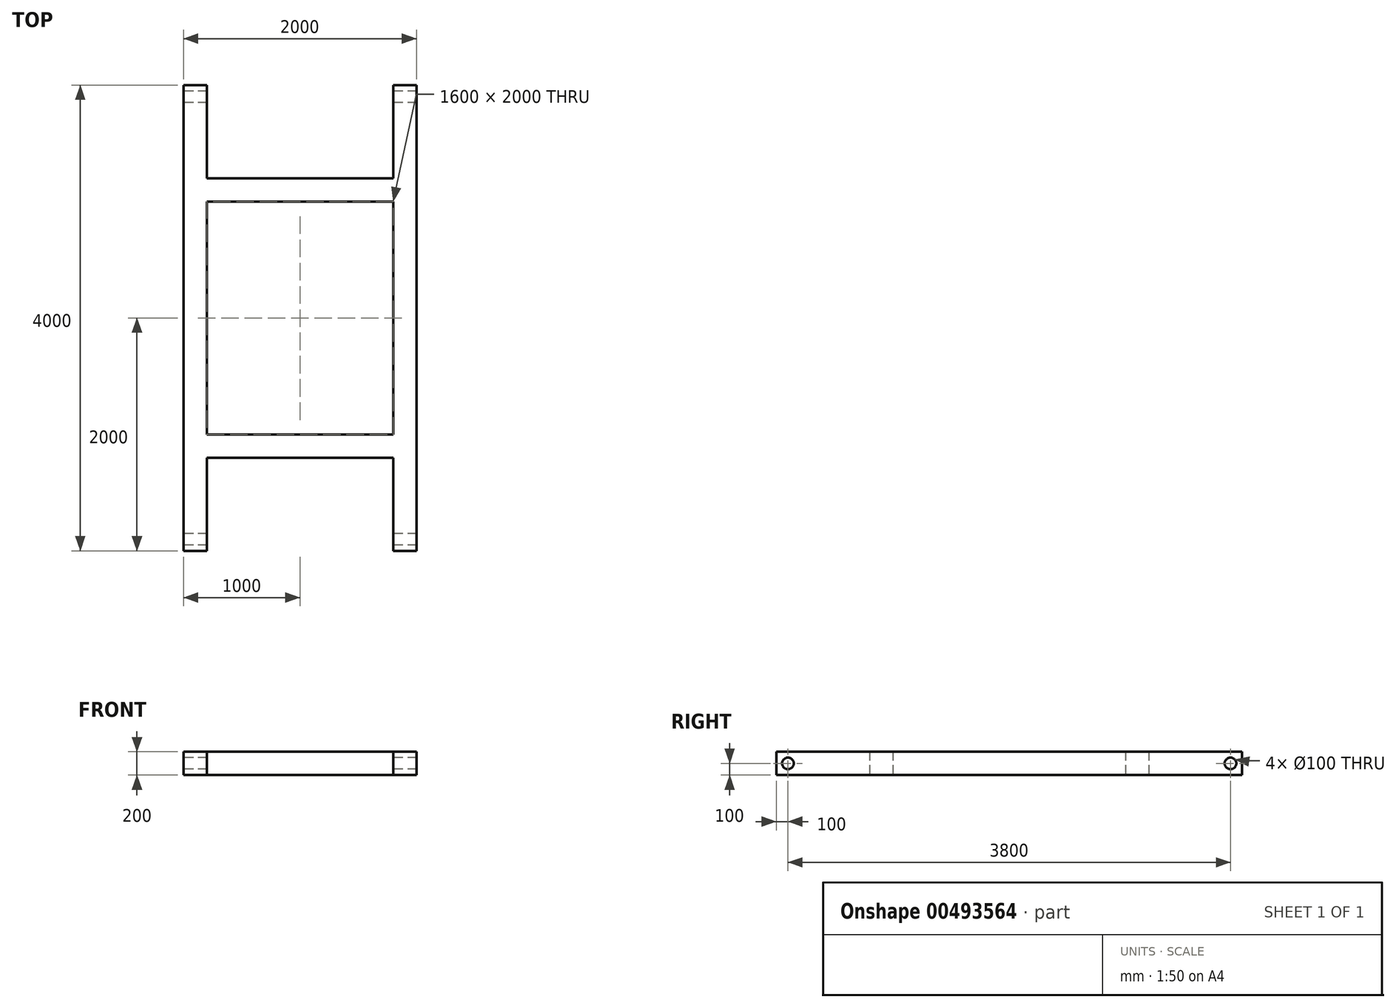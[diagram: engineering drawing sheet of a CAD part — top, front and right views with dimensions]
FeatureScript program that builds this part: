
annotation { "Feature Type Name" : "Feature", "Feature Type Description" : "" }
export const myFeature = defineFeature(function(context is Context, id is Id, definition is map)
    precondition{}
    {
        {
            var Q0;
            Q0=qCreatedBy(makeId("Top.planeOp"),FACE);
            var sketch = newSketch(context, id + "F0", { "sketchPlane" : qUnion([Q0])});
            skLineSegment(sketch, "E0", {"start": v(-1000, 2000) * mm, "end": v(-1000, -2000) * mm});
            skLineSegment(sketch, "E1", {"start": v(-1000, -2000) * mm, "end": v(-800, -2000) * mm});
            skLineSegment(sketch, "E2", {"start": v(-800, -2000) * mm, "end": v(-800, -1200) * mm});
            skLineSegment(sketch, "E3", {"start": v(-800, -1200) * mm, "end": v(800, -1200) * mm});
            skLineSegment(sketch, "E4", {"start": v(800, -1200) * mm, "end": v(800, -2000) * mm});
            skLineSegment(sketch, "E5", {"start": v(800, -2000) * mm, "end": v(1000, -2000) * mm});
            skLineSegment(sketch, "E6", {"start": v(1000, -2000) * mm, "end": v(1000, 2000) * mm});
            skLineSegment(sketch, "E7", {"start": v(-1000, 2000) * mm, "end": v(-800, 2000) * mm});
            skLineSegment(sketch, "E8", {"start": v(-800, 2000) * mm, "end": v(-800, 1200) * mm});
            skLineSegment(sketch, "E9", {"start": v(-800, 1200) * mm, "end": v(800, 1200) * mm});
            skLineSegment(sketch, "E10", {"start": v(800, 1200) * mm, "end": v(800, 2000) * mm});
            skLineSegment(sketch, "E11", {"start": v(800, 2000) * mm, "end": v(1000, 2000) * mm});
            skLineSegment(sketch, "E12", {"start": v(-800, 1000) * mm, "end": v(-800, -1000) * mm});
            skLineSegment(sketch, "E13", {"start": v(-800, -1000) * mm, "end": v(800, -1000) * mm});
            skLineSegment(sketch, "E14", {"start": v(800, -1000) * mm, "end": v(800, 1000) * mm});
            skLineSegment(sketch, "E15", {"start": v(-800, 1000) * mm, "end": v(800, 1000) * mm});
            skSolve(sketch);
        }
        {
            var Q0;
            Q0 = qSketchRegion(id + "F0", true);
            extrude(context, id + "F1", {"entities" : qUnion([Q0]), "depth" : 200 * mm});
        }
        {
            var Q0;
            Q0=makeQuery(id+"F1.opExtrude","SWEPT_FACE",FACE,{"disambiguationData":[OSD([sQuery(id+"F0.wireOp",EDGE,"E0")])]});
            var sketch = newSketch(context, id + "F2", { "sketchPlane" : qUnion([Q0])});
            skPoint(sketch, "E16", {"position": v(-1900, 100) * mm});
            skPoint(sketch, "E17", {"position": v(1900, 100) * mm});
            skSolve(sketch);
        }
        {
            var Q0;
            Q0=sQuery(id+"F2.wireOp",VERTEX,"E16");
            var Q1;
            Q1=sQuery(id+"F2.wireOp",VERTEX,"E17");
            var Q2;
            Q2=makeQuery(id+"F1.opExtrude","SWEPT_BODY",BODY,{"disambiguationData":[OSD([sQuery(id+"F0.wireOp",EDGE,"E0"),sQuery(id+"F0.wireOp",EDGE,"E1"),sQuery(id+"F0.wireOp",EDGE,"E2"),sQuery(id+"F0.wireOp",EDGE,"E3"),sQuery(id+"F0.wireOp",EDGE,"E4"),sQuery(id+"F0.wireOp",EDGE,"E5"),sQuery(id+"F0.wireOp",EDGE,"E6"),sQuery(id+"F0.wireOp",EDGE,"E7"),sQuery(id+"F0.wireOp",EDGE,"E8"),sQuery(id+"F0.wireOp",EDGE,"E9"),sQuery(id+"F0.wireOp",EDGE,"E10"),sQuery(id+"F0.wireOp",EDGE,"E11"),sQuery(id+"F0.wireOp",EDGE,"E12"),sQuery(id+"F0.wireOp",EDGE,"E13"),sQuery(id+"F0.wireOp",EDGE,"E14"),sQuery(id+"F0.wireOp",EDGE,"E15")])]});
            hole(context, id + "F3", {"style" : HoleStyle.SIMPLE, "endStyle" : HoleEndStyle.THROUGH, "holeDiameter" : 100 * mm, "isTappedThrough" : true, "tappedDepth" : 12 * mm, "tapClearance" : 3, "locations" : qUnion([Q0, Q1]), "scope" : qUnion([Q2])});
        }
    });
